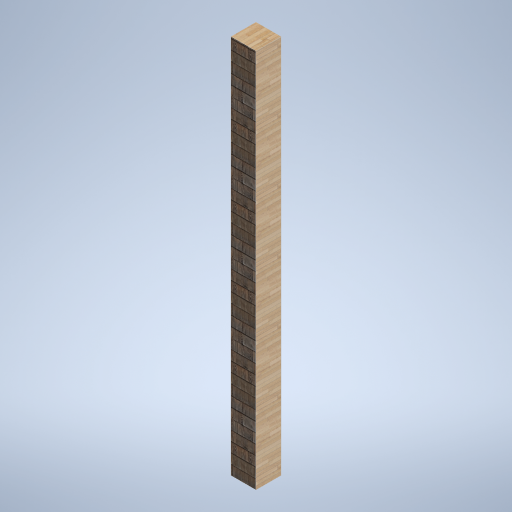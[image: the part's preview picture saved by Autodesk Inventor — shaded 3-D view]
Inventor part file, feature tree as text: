
AUTODESK INVENTOR PART (.ipt)
format: ipt  version: 2024.2 (Build 282272000, 272)  size: 309,760 bytes
history: native  units: in
note: dims shown in document units (in); Inventor stores cm internally (conversion verified against a paired STEP export)
features: other x3, sketch x1
ambient origin geometry x8: Origin, YZ Plane, XZ Plane, XY Plane, X Axis, Y Axis, Z Axis, Center Point
bodies: Solid1 (feature_tree)
feature tree (4):
  other  "support_frame_03.ipt"
  other  "Solid1::support_frame_03.ipt"
  other  "TaggingFeature1"
  sketch  "Sketch1"  dims[d0=0.3937in]
